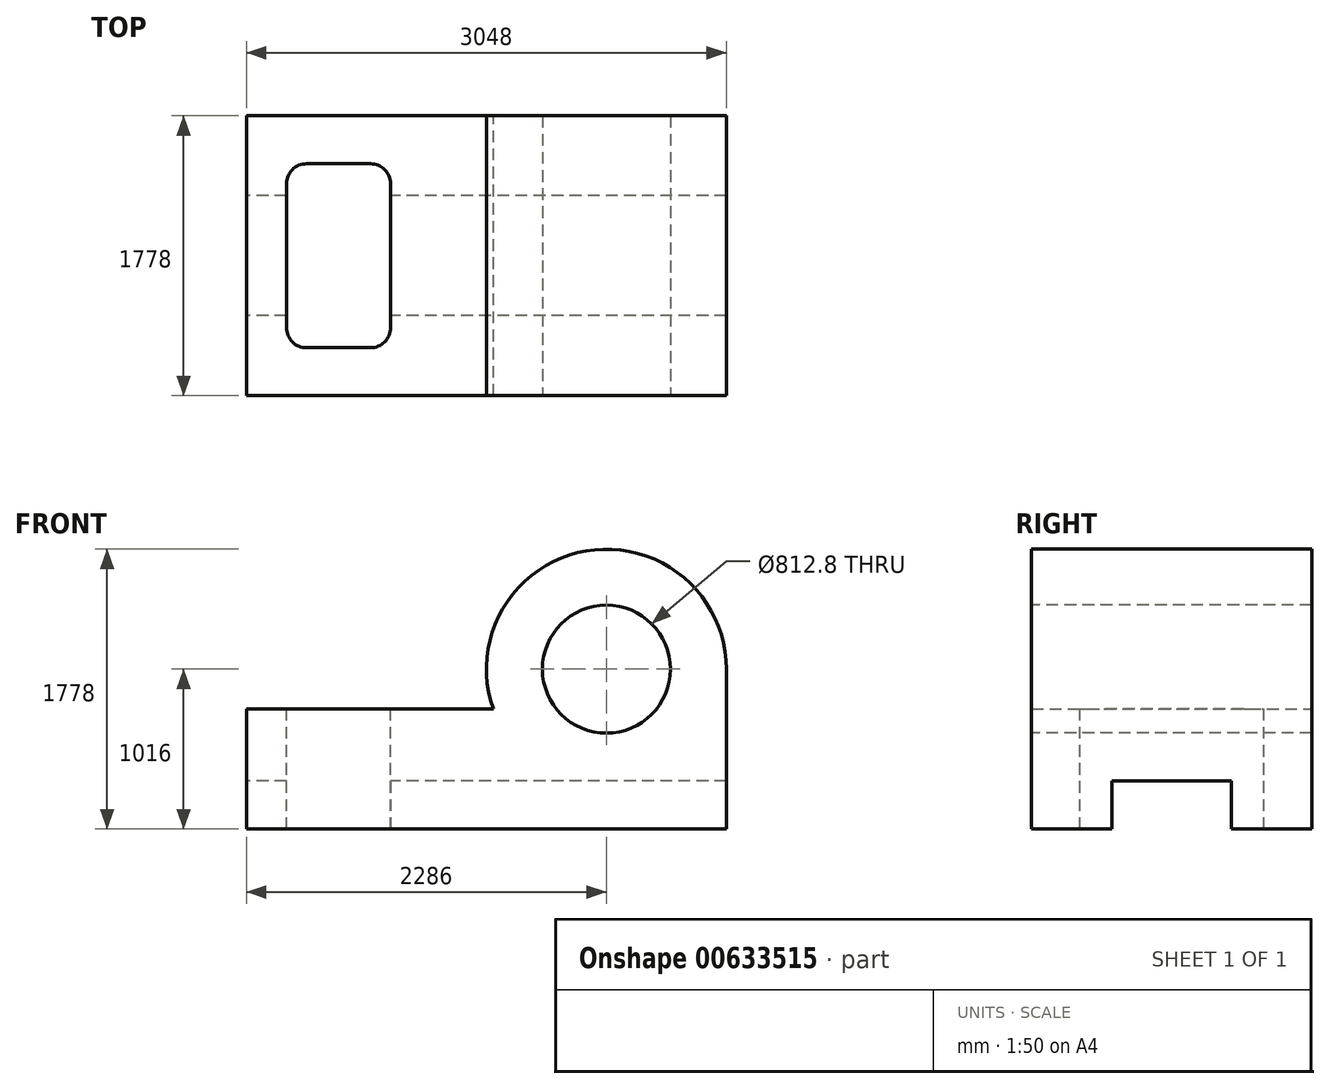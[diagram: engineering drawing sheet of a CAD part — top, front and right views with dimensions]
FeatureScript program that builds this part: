
annotation { "Feature Type Name" : "Feature", "Feature Type Description" : "" }
export const myFeature = defineFeature(function(context is Context, id is Id, definition is map)
    precondition{}
    {
        {
            var Q0;
            Q0=qCreatedBy(makeId("Front.planeOp"),FACE);
            var sketch = newSketch(context, id + "F0", { "sketchPlane" : qUnion([Q0])});
            skLineSegment(sketch, "E0.bottom", {"start": v(-1524, -381) * mm, "end": v(1524, -381) * mm});
            skLineSegment(sketch, "E0.top", {"start": v(-1524, 381) * mm, "end": v(1524, 381) * mm});
            skLineSegment(sketch, "E0.left", {"start": v(-1524, -381) * mm, "end": v(-1524, 381) * mm});
            skLineSegment(sketch, "E0.right", {"start": v(1524, -381) * mm, "end": v(1524, 381) * mm});
            skPoint(sketch, "E0.middle", {"position": v(0, 0) * mm});
            skLineSegment(sketch, "E1", {"start": v(-1524, -381) * mm, "end": v(762, -381) * mm});
            skLineSegment(sketch, "E2", {"start": v(1524, -381) * mm, "end": v(1524, 635) * mm});
            skLineSegment(sketch, "E3", {"start": v(762, -381) * mm, "end": v(762, -127) * mm});
            skCircle(sketch, "E4", {"center": v(762, 635) * mm, "radius": 762 * mm});
            skSolve(sketch);
        }
        {
            var Q0;
            Q0 = qSketchRegion(id + "F0", true);
            extrude(context, id + "F1", {"entities" : qUnion([Q0]), "depth" : 1778 * mm, "offsetDistance" : 25.4 * mm});
        }
        {
            var Q0;
            Q0=makeQuery(id+"F1.opExtrude","CAP_FACE",FACE,{"disambiguationData":[OSD([sQuery(id+"F0.wireOp",EDGE,"E0.bottom"),sQuery(id+"F0.wireOp",EDGE,"E0.top"),sQuery(id+"F0.wireOp",EDGE,"E0.left"),sQuery(id+"F0.wireOp",EDGE,"E1"),sQuery(id+"F0.wireOp",EDGE,"E2"),sQuery(id+"F0.wireOp",EDGE,"E4")])],"isStart":false});
            var sketch = newSketch(context, id + "F2", { "sketchPlane" : qUnion([Q0])});
            skLineSegment(sketch, "E5", {"start": v(1524, -381) * mm, "end": v(1524, 635) * mm});
            skLineSegment(sketch, "E6", {"start": v(1524, 635) * mm, "end": v(762, 635) * mm});
            skCircle(sketch, "E7", {"center": v(762, 635) * mm, "radius": 406.4 * mm});
            skSolve(sketch);
        }
        {
            var Q0;
            Q0 = qSketchRegion(id + "F2", true);
            extrude(context, id + "F3", {"entities" : qUnion([Q0]), "operationType" : NewBodyOperationType.ADD, "depth" : 25.4 * mm, "offsetDistance" : 25.4 * mm});
        }
        {
            var Q0;
            Q0=makeQuery(id+"F3.opExtrude","CAP_FACE",FACE,{"disambiguationData":[OSD([sQuery(id+"F2.wireOp",EDGE,"E7")])],"isStart":false});
            extrude(context, id + "F4", {"entities" : qUnion([Q0]), "operationType" : NewBodyOperationType.REMOVE, "endBound" : BoundingType.THROUGH_ALL, "oppositeDirection" : true, "depth" : 25.4 * mm, "offsetDistance" : 25.4 * mm});
        }
        {
            var Q0;
            Q0=makeQuery(id+"F1.opExtrude","SWEPT_FACE",FACE,{"disambiguationData":[OSD([sQuery(id+"F0.wireOp",EDGE,"E0.left")])]});
            var sketch = newSketch(context, id + "F5", { "sketchPlane" : qUnion([Q0])});
            skLineSegment(sketch, "E8", {"start": v(0, -381) * mm, "end": v(508, -381) * mm});
            skLineSegment(sketch, "E9", {"start": v(508, -381) * mm, "end": v(1270, -381) * mm});
            skLineSegment(sketch, "E10", {"start": v(1270, -381) * mm, "end": v(1778, -381) * mm});
            skLineSegment(sketch, "E11", {"start": v(508, -381) * mm, "end": v(508, -76.2) * mm});
            skLineSegment(sketch, "E12", {"start": v(508, -76.2) * mm, "end": v(1270, -76.2) * mm});
            skLineSegment(sketch, "E13", {"start": v(1270, -76.2) * mm, "end": v(1270, -381) * mm});
            skSolve(sketch);
        }
        {
            var Q0;
            Q0 = qSketchRegion(id + "F5", true);
            extrude(context, id + "F6", {"entities" : qUnion([Q0]), "operationType" : NewBodyOperationType.REMOVE, "endBound" : BoundingType.THROUGH_ALL, "oppositeDirection" : true, "depth" : 25.4 * mm, "offsetDistance" : 25.4 * mm});
        }
        {
            var Q0;
            Q0=makeQuery(id+"F1.opExtrude","SWEPT_FACE",FACE,{"disambiguationData":[OSD([sQuery(id+"F0.wireOp",EDGE,"E0.top")])]});
            var sketch = newSketch(context, id + "F7", { "sketchPlane" : qUnion([Q0])});
            skLineSegment(sketch, "E14", {"start": v(-1524, -1778) * mm, "end": v(-1270, -1778) * mm});
            skLineSegment(sketch, "E15", {"start": v(-1270, -1778) * mm, "end": v(-1270, -1473.2) * mm});
            skLineSegment(sketch, "E16", {"start": v(-1270, -1346.2) * mm, "end": v(-1270, -431.8) * mm});
            skLineSegment(sketch, "E17", {"start": v(-1143, -304.8) * mm, "end": v(-736.6, -304.8) * mm});
            skLineSegment(sketch, "E18", {"start": v(-609.6, -431.8) * mm, "end": v(-609.6, -1346.2) * mm});
            skLineSegment(sketch, "E19", {"start": v(-736.6, -1473.2) * mm, "end": v(-1143, -1473.2) * mm});
            skPoint(sketch, "E20.visualSharp", {"position": v(-1270, -304.8) * mm});
            skArc(sketch, "E20.filletArc", {"start": v(-1143, -304.8) * mm, "mid": v(-1232.8, -342) * mm, "end": v(-1270, -431.8) * mm});
            skPoint(sketch, "E21.visualSharp", {"position": v(-609.6, -304.8) * mm});
            skArc(sketch, "E21.filletArc", {"start": v(-609.6, -431.8) * mm, "mid": v(-646.8, -342) * mm, "end": v(-736.6, -304.8) * mm});
            skPoint(sketch, "E22.visualSharp", {"position": v(-609.6, -1473.2) * mm});
            skArc(sketch, "E22.filletArc", {"start": v(-736.6, -1473.2) * mm, "mid": v(-646.8, -1436) * mm, "end": v(-609.6, -1346.2) * mm});
            skPoint(sketch, "E23.visualSharp", {"position": v(-1270, -1473.2) * mm});
            skArc(sketch, "E23.filletArc", {"start": v(-1270, -1346.2) * mm, "mid": v(-1232.8, -1436) * mm, "end": v(-1143, -1473.2) * mm});
            skSolve(sketch);
        }
        {
            var Q0;
            Q0 = qSketchRegion(id + "F7", true);
            extrude(context, id + "F8", {"entities" : qUnion([Q0]), "operationType" : NewBodyOperationType.REMOVE, "endBound" : BoundingType.THROUGH_ALL, "oppositeDirection" : true, "depth" : 25.4 * mm, "offsetDistance" : 25.4 * mm});
        }
    });
